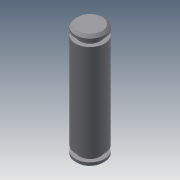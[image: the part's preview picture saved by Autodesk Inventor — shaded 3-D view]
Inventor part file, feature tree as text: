
AUTODESK INVENTOR PART (.ipt)
format: ipt  version: 2013 (Build 170138000, 138)  size: 100,352 bytes
history: native  units: mm
features: sketch x3, extrude x2, revolve x1, chamfer x1
ambient origin geometry x8: Origin, YZ Plane, XZ Plane, XY Plane, X Axis, Y Axis, Z Axis, Center Point
bodies: Solid1 (feature_tree)
feature tree (7):
  revolve  "Revolution1"  [1 undecoded]
  extrude  "Extrusion1"  Depth=1.0mm
  extrude  "Extrusion2"  Depth=0.25mm TaperAngle=0.0deg
  chamfer  "Chamfer1"  Distance=0.25mm
  sketch  "Sketch1"  dims[d12=19.5mm d13=1.0mm]
  sketch  "Sketch2"  dims[d14=0.85mm d16=1.0mm]
  sketch  "Sketch3"  dims[d17=90.0deg d18=0.25mm d19=0.0mm d20=0.25mm d21=0.0mm d22=0.5mm d23=2.0mm d24=45.0deg]
note: 1 required parameter value undecoded (feature->parameter linkage not recoverable at this tier; creation-order binding heuristic only, values carry confidence <= 0.55)
